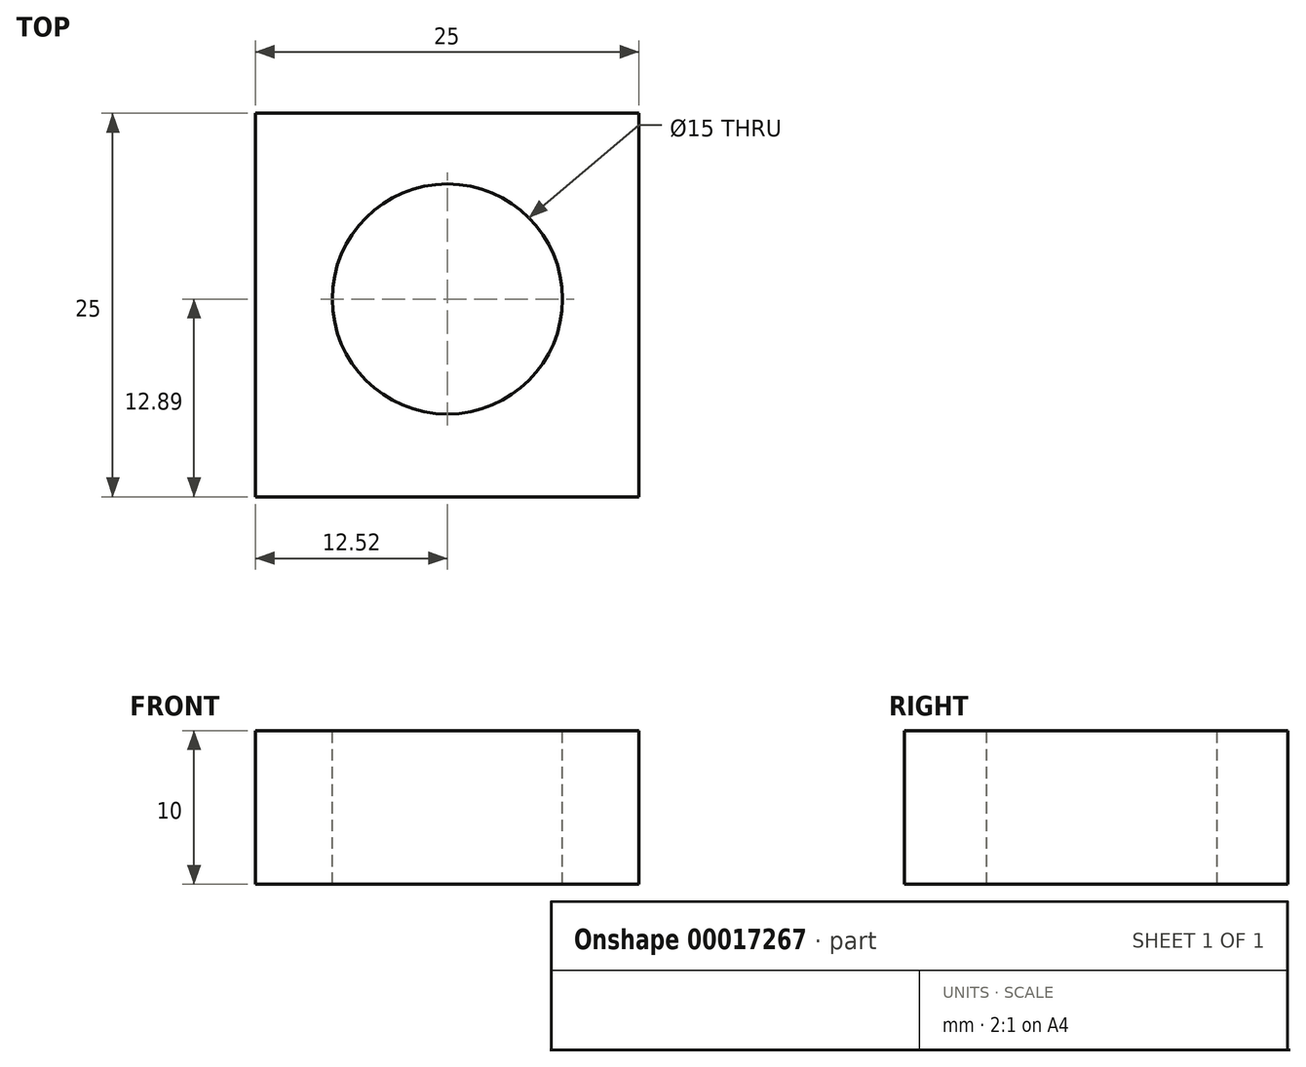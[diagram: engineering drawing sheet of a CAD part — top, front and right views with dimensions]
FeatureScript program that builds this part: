
annotation { "Feature Type Name" : "Feature", "Feature Type Description" : "" }
export const myFeature = defineFeature(function(context is Context, id is Id, definition is map)
    precondition{}
    {
        {
            var Q0;
            Q0=qCreatedBy(makeId("Top.planeOp"),FACE);
            var sketch = newSketch(context, id + "F0", { "sketchPlane" : qUnion([Q0])});
            skLineSegment(sketch, "E0", {"start": v(-12.52, 12.1) * mm, "end": v(-12.52, -12.9) * mm});
            skLineSegment(sketch, "E1", {"start": v(-12.52, -12.9) * mm, "end": v(12.48, -12.9) * mm});
            skLineSegment(sketch, "E2", {"start": v(12.48, -12.9) * mm, "end": v(12.48, 12.1) * mm});
            skLineSegment(sketch, "E3", {"start": v(12.48, 12.1) * mm, "end": v(-12.52, 12.1) * mm});
            skSolve(sketch);
        }
        {
            var Q0;
            Q0 = qSketchRegion(id + "F0", true);
            extrude(context, id + "F1", {"entities" : qUnion([Q0]), "depth" : 10 * mm});
        }
        {
            var Q0;
            Q0=makeQuery(id+"F1.opExtrude","CAP_FACE",FACE,{"disambiguationData":[OSD([sQuery(id+"F0.wireOp",EDGE,"E0"),sQuery(id+"F0.wireOp",EDGE,"E1"),sQuery(id+"F0.wireOp",EDGE,"E2"),sQuery(id+"F0.wireOp",EDGE,"E3")])],"isStart":false});
            var sketch = newSketch(context, id + "F2", { "sketchPlane" : qUnion([Q0])});
            skCircle(sketch, "E4", {"center": v(0, 0) * mm, "radius": 7.5 * mm});
            skSolve(sketch);
        }
        {
            var Q0;
            Q0=makeQuery(id+"F2.imprint","IMPRINT",FACE,{"disambiguationData":[TD([[makeQuery(id+"F2.imprint","IMPRINT",EDGE,{"derivedFrom":sQuery(id+"F2.wireOp",EDGE,"E4")}),1.0]])]});
            extrude(context, id + "F3", {"entities" : qUnion([Q0]), "operationType" : NewBodyOperationType.REMOVE, "endBound" : BoundingType.THROUGH_ALL, "oppositeDirection" : true, "depth" : 25 * mm});
        }
    });
